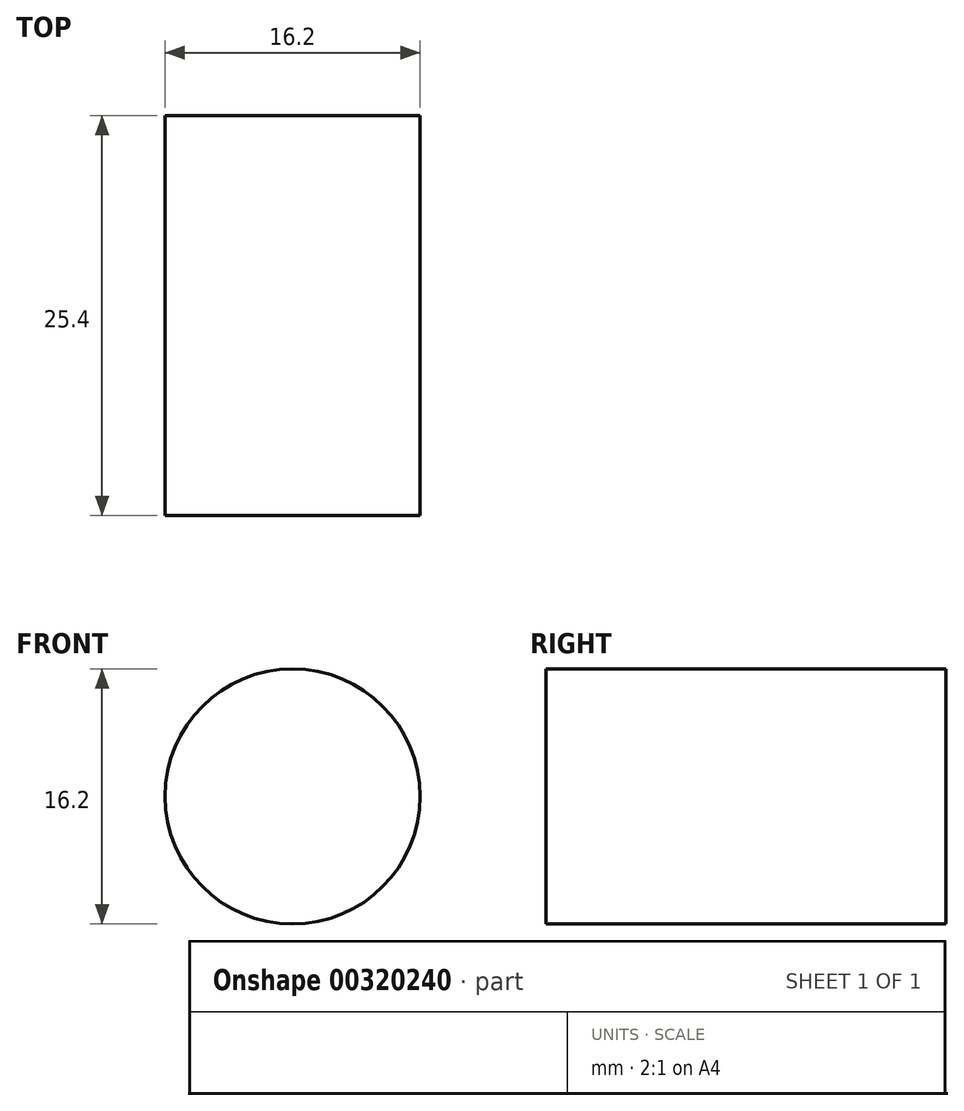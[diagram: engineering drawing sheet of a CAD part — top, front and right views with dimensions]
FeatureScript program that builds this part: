
annotation { "Feature Type Name" : "Feature", "Feature Type Description" : "" }
export const myFeature = defineFeature(function(context is Context, id is Id, definition is map)
    precondition{}
    {
        {
            var Q0;
            Q0=qCreatedBy(makeId("Front.planeOp"),FACE);
            var sketch = newSketch(context, id + "F0", { "sketchPlane" : qUnion([Q0])});
            skCircle(sketch, "E0", {"center": v(0, 0) * mm, "radius": 8.1 * mm});
            skSolve(sketch);
        }
        {
            var Q0;
            Q0=makeQuery(id+"F0.imprint","IMPRINT",FACE,{"disambiguationData":[TD([[makeQuery(id+"F0.imprint","IMPRINT",EDGE,{"derivedFrom":sQuery(id+"F0.wireOp",EDGE,"E0")}),1.0]])]});
            extrude(context, id + "F1", {"entities" : qUnion([Q0]), "endBound" : BoundingType.SYMMETRIC, "depth" : 25.4 * mm});
        }
    });
